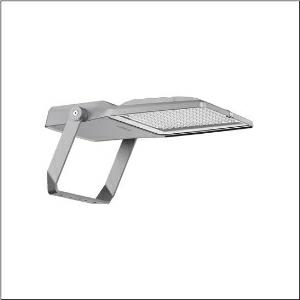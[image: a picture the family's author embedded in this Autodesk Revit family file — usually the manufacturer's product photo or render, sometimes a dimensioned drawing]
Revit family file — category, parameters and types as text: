
# Revit family: floodlight_fl_21_iq_midi___rs12_5xa7781f6b1a_422c
name_source: partatom
category: Lighting Fixtures
units: mm (PartAtom-declared; Revit-internal decimal feet)

## family parameters
Cut with Voids When Loaded = No
Host = Face
Light Source = No
Part Type = Normal
Room Calculation Point = No
Round Connector Dimension = Use Diameter
Shared = No

## types (1)
- --- (1 x LED, 28520 lm, 270.2 W, 5700K)
    Apparent Load = 270 VA
    CIE Flux Codes = 79 92 99 100 100
    Color Rendering = 90
    Color Temperature = 5700K
    Default Elevation = 1800 mm
    Description = Floodlight FL 21 iQ midi, floodlight, primary light control with lens, of PMMA, primary optical cover: protective disc, of toughened safety glass, transparent, light distribution: RS12, light emission: direct distribution, installation type: surface-mounted, LED, High Power LED, rated luminous flux: 28.520lm, luminous efficacy: 106lm/W, light colour: 957, colour temperature: 5700K, control gear: iQ Comfort/DALI, control: optimised constant luminous flux control (CLO 2.0), Desk-Remote (wireless, voltage-free reading and setting of iQ features in the workshop via application-optimized NFC function/RFID function), Light-Fading, Smart-Wire, Night-Set, Lumen-Switch, Temp-Guard, Auto-Match, with terminal, 6-pole, mains connection: 220..240V, AC, 50/60Hz, start of lifetime: 270W, end of service life: 287W, reduction: 117W, luminaire housing, of diecast aluminium, powder-coated, Siteco® metallic grey (DB 702S), corrosivity category C5 mid according to DIN EN ISO 12944, suitable for swimming pools, chlorine-resistant, sealing non-destructively replaceable, mounting bracket, of steel, galvanised, powder-coated, Siteco® metallic grey (DB 702S), protection rating (complete): IP66, insulation class (complete): insulation class II (safety insulation), certification: CE, ENEC, VDE, protection symbol: D, impact resistance: IK08, permissible operating ambient temperature: -40..+40°C, permissible operating ambient temperature for outdoor applications: -40..+50°C, standard: DIN EN 12944, LABS conformity tested according to VDMA 24364:2018-05, packaging unit: 1 piece

Light Distribution: RS12
    Height = 76 mm
    Lamp = 1 x LED
    Lamp Light Flux = 28520 lm
    Lamp Power = 270.2 W
    Lamp count = 1
    Length = 657 mm
    Luminous efficacy = 106 lm/W
    Manufacturer = Siteco
    ModVariant = No
    Model = 5XA7781F6B1A
    Number of Poles = 1
    OnlyDefault = Yes
    Power Factor = 1
    Product Name = Floodlight FL 21 iQ midi | RS12
    Product group = floodlight | pylon annexe
    ProductGroupID = 6201
    Protection Class = Protection class II
    Protection Degree = IP 66
    RLX_Detail_Level = 1
    RLX_Emergency_Light_Flux = 0 lm
    RLX_Emergency_Type = 0
    RLX_Emergency_Type_DB = No
    RlxData = <blob elided: 141265 chars, md5=a456711d>
    Socket = socket
    Standby Power = 0 W
    System Light Flux = 28520 lm
    System Power = 270 W
    Type Comments = factory setting: luminous flux: 100 % | dim-lin: 254 | 620 mA
    Type Image = l_1006876.jpg
    URL = http://relux.com
    VarID = @adj_128795
    Voltage = 0 V
    Weight = 0.00 kg
    Width = 442 mm

## geometry (parser evidence)
native form markers: Blend x4, Sweep x11
no freeform markers — native parametric forms only
